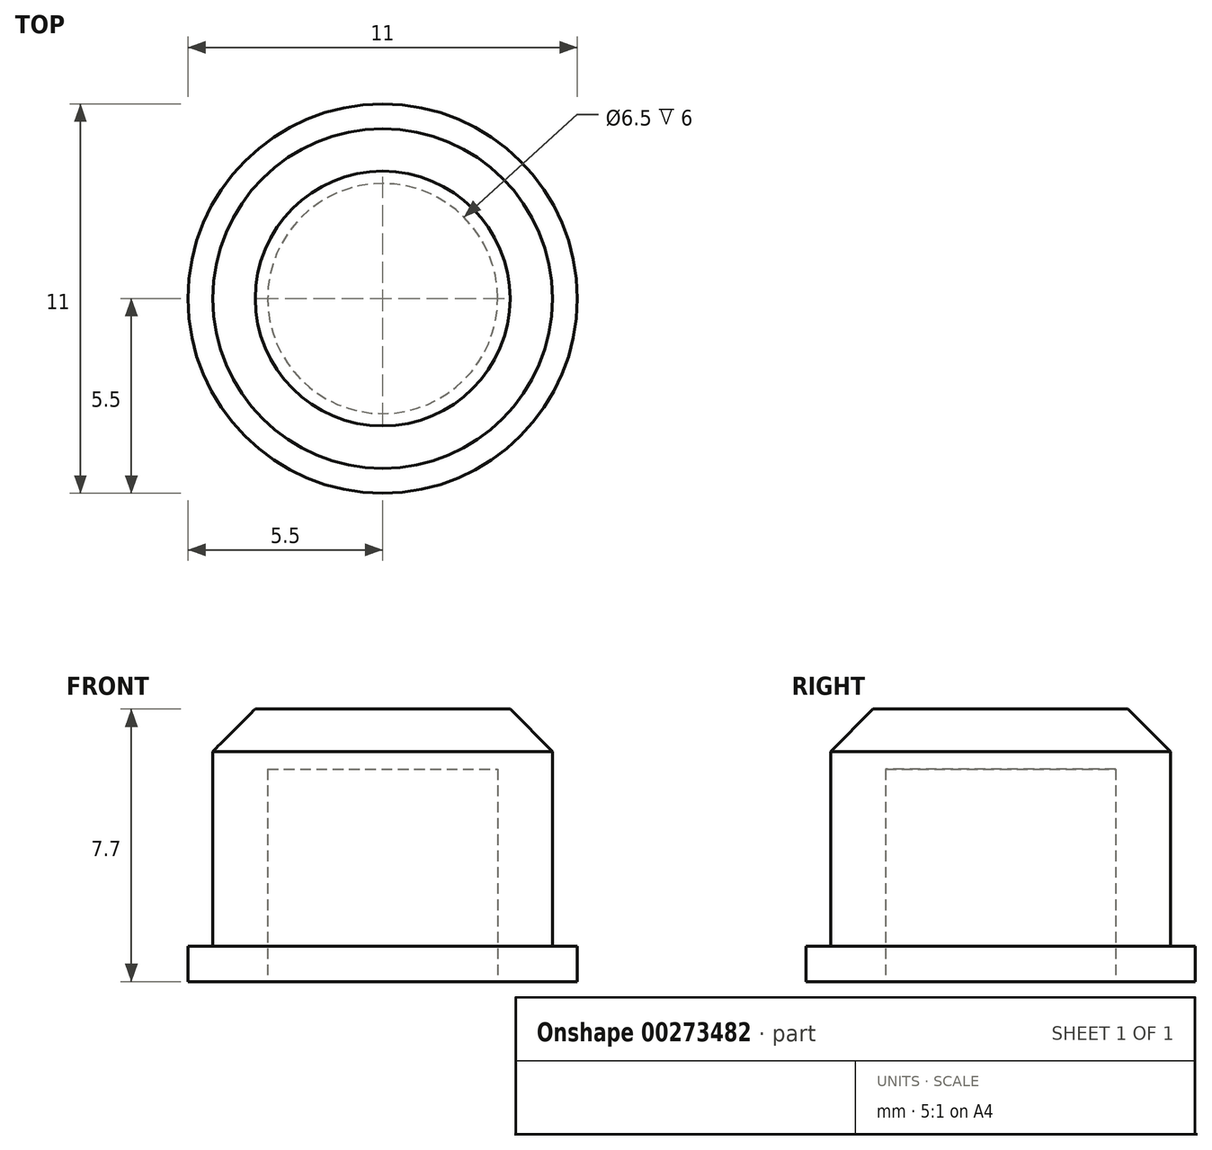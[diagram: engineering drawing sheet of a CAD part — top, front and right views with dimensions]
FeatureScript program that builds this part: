
annotation { "Feature Type Name" : "Feature", "Feature Type Description" : "" }
export const myFeature = defineFeature(function(context is Context, id is Id, definition is map)
    precondition{}
    {
        {
            var Q0;
            Q0=qCreatedBy(makeId("Front.planeOp"),FACE);
            var sketch = newSketch(context, id + "F0", { "sketchPlane" : qUnion([Q0])});
            skLineSegment(sketch, "E0", {"start": v(-5.5, 0) * mm, "end": v(-5.5, 1) * mm});
            skLineSegment(sketch, "E1", {"start": v(-5.5, 1) * mm, "end": v(-4.8, 1) * mm});
            skLineSegment(sketch, "E2", {"start": v(-4.8, 1) * mm, "end": v(-4.8, 6.5) * mm});
            skLineSegment(sketch, "E3", {"start": v(-4.8, 6.5) * mm, "end": v(-3.6, 7.7) * mm});
            skLineSegment(sketch, "E4", {"start": v(-3.6, 7.7) * mm, "end": v(0, 7.7) * mm});
            skLineSegment(sketch, "E5", {"start": v(-5.5, 0) * mm, "end": v(-3.25, 0) * mm});
            skLineSegment(sketch, "E6", {"start": v(-3.25, 0) * mm, "end": v(-3.25, 6) * mm});
            skLineSegment(sketch, "E7", {"start": v(-3.25, 6) * mm, "end": v(0, 6) * mm});
            skLineSegment(sketch, "E8", {"start": v(0, 0) * mm, "end": v(0, 9.38) * mm, "construction": true});
            skLineSegment(sketch, "E9", {"start": v(0, 7.7) * mm, "end": v(0, 6) * mm});
            skSolve(sketch);
        }
        {
            var Q0;
            Q0 = qSketchRegion(id + "F0", true);
            var Q1;
            Q1=sQuery(id+"F0.wireOp",EDGE,"E8");
            revolve(context, id + "F1", {"entities" : qUnion([Q0]), "axis" : qUnion([Q1]), "revolveType" : RevolveType.FULL});
        }
    });
